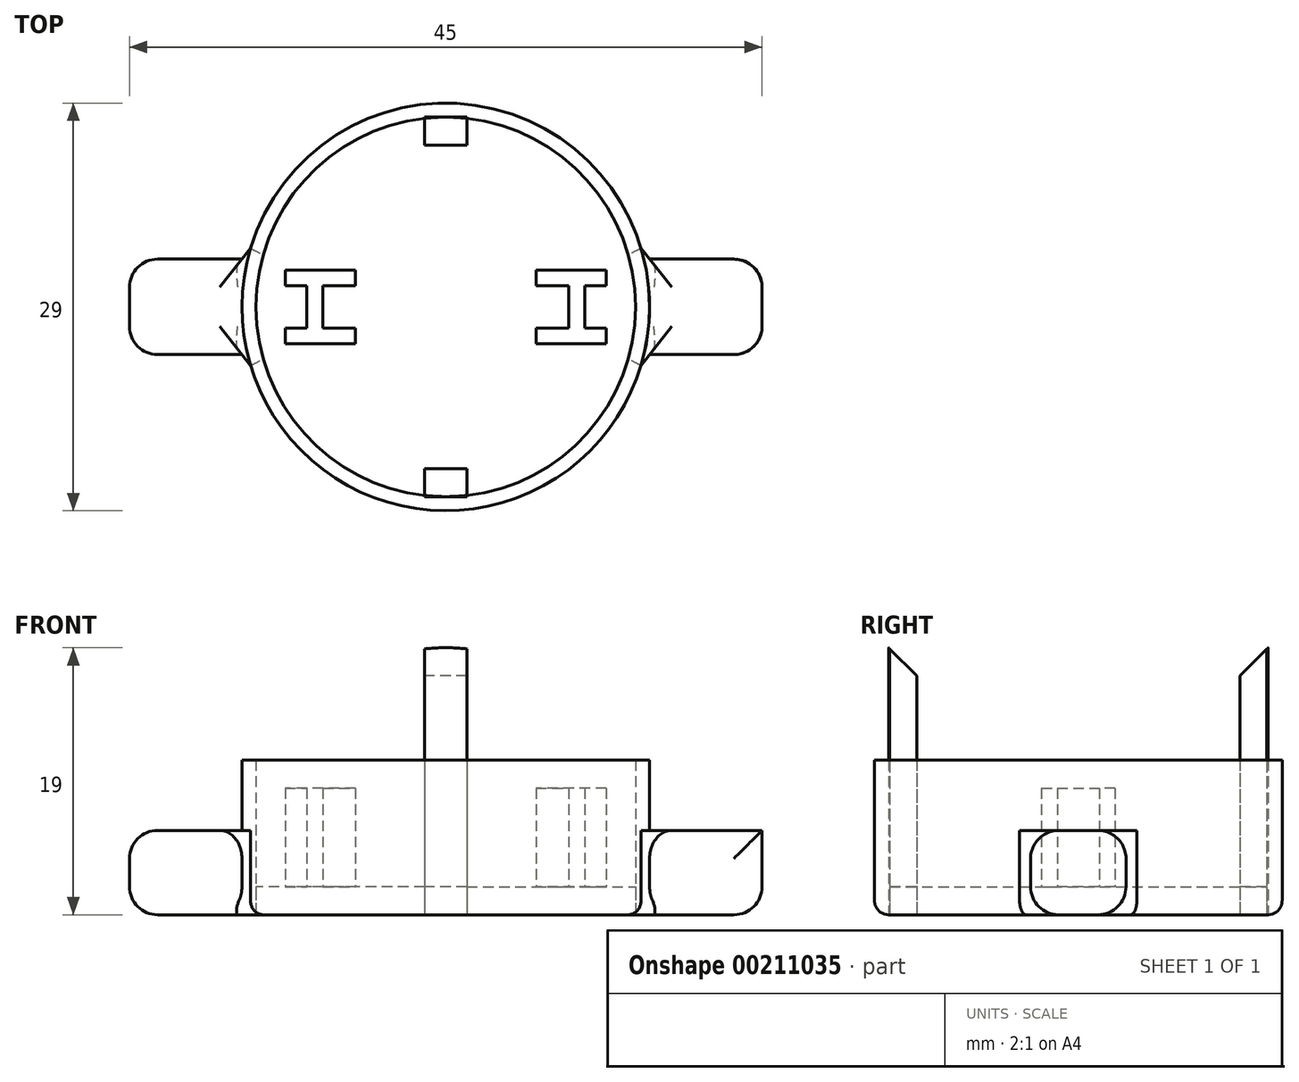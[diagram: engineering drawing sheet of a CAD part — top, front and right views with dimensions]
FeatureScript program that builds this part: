
annotation { "Feature Type Name" : "Feature", "Feature Type Description" : "" }
export const myFeature = defineFeature(function(context is Context, id is Id, definition is map)
    precondition{}
    {
        {
            var Q0;
            Q0=qCreatedBy(makeId("Top.planeOp"),FACE);
            var sketch = newSketch(context, id + "F0", { "sketchPlane" : qUnion([Q0])});
            skCircle(sketch, "E0", {"center": v(0, 0) * mm, "radius": 14.5 * mm});
            skCircle(sketch, "E1", {"center": v(0, 0) * mm, "radius": 13.5 * mm});
            skLineSegment(sketch, "E2", {"start": v(0, 13.5) * mm, "end": v(1.5, 13.5) * mm});
            skLineSegment(sketch, "E3", {"start": v(1.5, 13.5) * mm, "end": v(1.5, 11.5) * mm});
            skLineSegment(sketch, "E4", {"start": v(1.5, 11.5) * mm, "end": v(-1.5, 11.5) * mm});
            skLineSegment(sketch, "E5", {"start": v(-1.5, 11.5) * mm, "end": v(-1.5, 13.5) * mm});
            skLineSegment(sketch, "E6", {"start": v(-1.5, 13.5) * mm, "end": v(0, 13.5) * mm});
            skLineSegment(sketch, "E7", {"start": v(0, -13.5) * mm, "end": v(1.5, -13.5) * mm});
            skLineSegment(sketch, "E8", {"start": v(1.5, -13.5) * mm, "end": v(1.5, -11.5) * mm});
            skLineSegment(sketch, "E9", {"start": v(1.5, -11.5) * mm, "end": v(-1.5, -11.5) * mm});
            skLineSegment(sketch, "E10", {"start": v(-1.5, -11.5) * mm, "end": v(-1.5, -13.5) * mm});
            skLineSegment(sketch, "E11", {"start": v(-1.5, -13.5) * mm, "end": v(0, -13.5) * mm});
            skLineSegment(sketch, "E12", {"start": v(0, 15.56) * mm, "end": v(0, -16.2) * mm, "construction": true});
            skLineSegment(sketch, "E13", {"start": v(-9.9, 0) * mm, "end": v(-9.9, 1.5) * mm});
            skLineSegment(sketch, "E14", {"start": v(-9.9, 1.5) * mm, "end": v(-11.42, 1.5) * mm});
            skLineSegment(sketch, "E15", {"start": v(-11.42, 1.5) * mm, "end": v(-11.42, 2.62) * mm});
            skLineSegment(sketch, "E16", {"start": v(-11.42, 2.62) * mm, "end": v(-6.42, 2.62) * mm});
            skLineSegment(sketch, "E17", {"start": v(-6.42, 2.62) * mm, "end": v(-6.42, 1.5) * mm});
            skLineSegment(sketch, "E18", {"start": v(-6.42, 1.5) * mm, "end": v(-8.75, 1.5) * mm});
            skLineSegment(sketch, "E19", {"start": v(-8.75, 1.5) * mm, "end": v(-8.75, -1.5) * mm});
            skLineSegment(sketch, "E20", {"start": v(-8.75, -1.5) * mm, "end": v(-6.42, -1.5) * mm});
            skLineSegment(sketch, "E21", {"start": v(-6.42, -1.5) * mm, "end": v(-6.42, -2.62) * mm});
            skLineSegment(sketch, "E22", {"start": v(-6.42, -2.62) * mm, "end": v(-11.42, -2.62) * mm});
            skLineSegment(sketch, "E23", {"start": v(-11.42, -2.62) * mm, "end": v(-11.42, -1.5) * mm});
            skLineSegment(sketch, "E24", {"start": v(-11.42, -1.5) * mm, "end": v(-9.9, -1.5) * mm});
            skLineSegment(sketch, "E25", {"start": v(-9.9, -1.5) * mm, "end": v(-9.9, 0) * mm});
            skLineSegment(sketch, "E26.MirrorCS", {"start": v(9.9, 1.5) * mm, "end": v(11.42, 1.5) * mm});
            skLineSegment(sketch, "E27.MirrorCS", {"start": v(9.9, 0) * mm, "end": v(9.9, 1.5) * mm});
            skLineSegment(sketch, "E28.MirrorCS", {"start": v(11.42, 2.62) * mm, "end": v(6.42, 2.62) * mm});
            skLineSegment(sketch, "E29.MirrorCS", {"start": v(6.42, 1.5) * mm, "end": v(8.75, 1.5) * mm});
            skLineSegment(sketch, "E30.MirrorCS", {"start": v(8.75, -1.5) * mm, "end": v(6.42, -1.5) * mm});
            skLineSegment(sketch, "E31.MirrorCS", {"start": v(6.42, -2.62) * mm, "end": v(11.42, -2.62) * mm});
            skLineSegment(sketch, "E32.MirrorCS", {"start": v(11.42, -2.62) * mm, "end": v(11.42, -1.5) * mm});
            skLineSegment(sketch, "E33.MirrorCS", {"start": v(11.42, -1.5) * mm, "end": v(9.9, -1.5) * mm});
            skLineSegment(sketch, "E34.MirrorCS", {"start": v(6.42, -1.5) * mm, "end": v(6.42, -2.62) * mm});
            skLineSegment(sketch, "E35.MirrorCS", {"start": v(9.9, -1.5) * mm, "end": v(9.9, 0) * mm});
            skLineSegment(sketch, "E36.MirrorCS", {"start": v(11.42, 1.5) * mm, "end": v(11.42, 2.62) * mm});
            skLineSegment(sketch, "E37.MirrorCS", {"start": v(6.42, 2.62) * mm, "end": v(6.42, 1.5) * mm});
            skLineSegment(sketch, "E38.MirrorCS", {"start": v(8.75, 1.5) * mm, "end": v(8.75, -1.5) * mm});
            skLineSegment(sketch, "E39", {"start": v(-14.5, 0) * mm, "end": v(-14.5, 3.4) * mm});
            skLineSegment(sketch, "E40", {"start": v(-14.5, 3.4) * mm, "end": v(-22.5, 3.4) * mm});
            skLineSegment(sketch, "E41", {"start": v(-22.5, 3.4) * mm, "end": v(-22.5, -3.4) * mm});
            skLineSegment(sketch, "E42", {"start": v(-22.5, -3.4) * mm, "end": v(-14.5, -3.4) * mm});
            skLineSegment(sketch, "E43", {"start": v(-14.5, -3.4) * mm, "end": v(-14.5, 0) * mm});
            skLineSegment(sketch, "E44", {"start": v(-14.5, -3.4) * mm, "end": v(-13.89, -4.18) * mm});
            skLineSegment(sketch, "E45", {"start": v(-14.5, 3.4) * mm, "end": v(-13.89, 4.17) * mm});
            skLineSegment(sketch, "E46.MirrorCS", {"start": v(14.5, 3.4) * mm, "end": v(13.89, 4.17) * mm});
            skLineSegment(sketch, "E47.MirrorCS", {"start": v(14.5, 3.4) * mm, "end": v(22.5, 3.4) * mm});
            skLineSegment(sketch, "E48.MirrorCS", {"start": v(14.5, 0) * mm, "end": v(14.5, 3.4) * mm});
            skLineSegment(sketch, "E49.MirrorCS", {"start": v(22.5, 3.4) * mm, "end": v(22.5, -3.4) * mm});
            skLineSegment(sketch, "E50.MirrorCS", {"start": v(22.5, -3.4) * mm, "end": v(14.5, -3.4) * mm});
            skLineSegment(sketch, "E51.MirrorCS", {"start": v(14.5, -3.4) * mm, "end": v(14.5, 0) * mm});
            skLineSegment(sketch, "E52.MirrorCS", {"start": v(14.5, -3.4) * mm, "end": v(13.89, -4.18) * mm});
            skSolve(sketch);
        }
        {
            var Q0;
            Q0=makeQuery(id+"F0.imprint","IMPRINT",FACE,{"disambiguationData":[TD([[makeQuery(id+"F0.imprint","IMPRINT",EDGE,{"derivedFrom":sQuery(id+"F0.wireOp",EDGE,"E13")}),-1.0]])]});
            var Q1;
            {var subQ4=sQuery(id+"F0.wireOp",EDGE,"E4");Q1=makeQuery(id+"F0.imprint","IMPRINT",FACE,{"disambiguationData":[TD([[makeQuery(id+"F0.imprint","IMPRINT",EDGE,{"derivedFrom":subQ4}),1.0]])]});}
            var Q2;
            Q2=makeQuery(id+"F0.imprint","IMPRINT",FACE,{"disambiguationData":[TD([[makeQuery(id+"F0.imprint","IMPRINT",EDGE,{"derivedFrom":sQuery(id+"F0.wireOp",EDGE,"E26.MirrorCS")}),1.0]])]});
            extrude(context, id + "F1", {"entities" : qUnion([Q0, Q1, Q2]), "depth" : 2 * mm});
        }
        {
            var Q0;
            {var subQ1=sQuery(id+"F0.wireOp",EDGE,"E2");Q0=makeQuery(id+"F0.imprint","IMPRINT",FACE,{"disambiguationData":[TD([[makeQuery(id+"F0.imprint","IMPRINT",EDGE,{"derivedFrom":subQ1}),1.0]])]});}
            var Q1;
            Q1=makeQuery(id+"F1.opExtrude","CAP_FACE",FACE,{"disambiguationData":[OSD([sQuery(id+"F0.wireOp",EDGE,"E1")])],"isStart":false});
            extrude(context, id + "F2", {"entities" : qUnion([Q0]), "depth" : 11 * mm});
        }
        {
            var Q0;
            Q0=makeQuery(id+"F0.imprint","IMPRINT",FACE,{"disambiguationData":[TD([[makeQuery(id+"F0.imprint","IMPRINT",EDGE,{"derivedFrom":sQuery(id+"F0.wireOp",EDGE,"E13")}),-1.0]])]});
            var Q1;
            Q1=makeQuery(id+"F0.imprint","IMPRINT",FACE,{"disambiguationData":[TD([[makeQuery(id+"F0.imprint","IMPRINT",EDGE,{"derivedFrom":sQuery(id+"F0.wireOp",EDGE,"E26.MirrorCS")}),1.0]])]});
            extrude(context, id + "F3", {"entities" : qUnion([Q0, Q1]), "operationType" : NewBodyOperationType.ADD, "depth" : 9 * mm});
        }
        {
            var Q0;
            {var subQ0=sQuery(id+"F0.wireOp",EDGE,"E9");Q0=makeQuery(id+"F0.imprint","IMPRINT",FACE,{"disambiguationData":[TD([[makeQuery(id+"F0.imprint","IMPRINT",EDGE,{"derivedFrom":subQ0}),1.0]])]});}
            var Q1;
            {var subQ0=sQuery(id+"F0.wireOp",EDGE,"E4");Q1=makeQuery(id+"F0.imprint","IMPRINT",FACE,{"disambiguationData":[TD([[makeQuery(id+"F0.imprint","IMPRINT",EDGE,{"derivedFrom":subQ0}),-1.0]])]});}
            var Q2;
            Q2=makeQuery(id+"F1.opExtrude","CAP_FACE",FACE,{"disambiguationData":[OSD([sQuery(id+"F0.wireOp",EDGE,"E1")])],"isStart":false});
            var Q3;
            Q3=makeQuery(id+"F1.opExtrude","SWEPT_BODY",BODY,{"disambiguationData":[OSD([sQuery(id+"F0.wireOp",EDGE,"E1")])]});
            extrude(context, id + "F4", {"entities" : qUnion([Q0, Q1]), "depth" : 19 * mm});
        }
        {
            var Q0;
            Q0=makeQuery(id+"F0.imprint","IMPRINT",FACE,{"disambiguationData":[TD([[makeQuery(id+"F0.imprint","IMPRINT",EDGE,{"derivedFrom":sQuery(id+"F0.wireOp",EDGE,"E39")}),1.0]])]});
            var Q1;
            Q1=makeQuery(id+"F0.imprint","IMPRINT",FACE,{"disambiguationData":[TD([[makeQuery(id+"F0.imprint","IMPRINT",EDGE,{"derivedFrom":sQuery(id+"F0.wireOp",EDGE,"E47.MirrorCS")}),-1.0]])]});
            var Q2;
            {var subQ0=sQuery(id+"F0.wireOp",EDGE,"E43");Q2=makeQuery(id+"F0.imprint","IMPRINT",FACE,{"disambiguationData":[TD([[makeQuery(id+"F0.imprint","IMPRINT",EDGE,{"derivedFrom":subQ0}),-1.0]])]});}
            var Q3;
            {var subQ0=sQuery(id+"F0.wireOp",EDGE,"E39");Q3=makeQuery(id+"F0.imprint","IMPRINT",FACE,{"disambiguationData":[TD([[makeQuery(id+"F0.imprint","IMPRINT",EDGE,{"derivedFrom":subQ0}),-1.0]])]});}
            var Q4;
            {var subQ0=sQuery(id+"F0.wireOp",EDGE,"E51.MirrorCS");Q4=makeQuery(id+"F0.imprint","IMPRINT",FACE,{"disambiguationData":[TD([[makeQuery(id+"F0.imprint","IMPRINT",EDGE,{"derivedFrom":subQ0}),1.0]])]});}
            var Q5;
            {var subQ0=sQuery(id+"F0.wireOp",EDGE,"E46.MirrorCS");Q5=makeQuery(id+"F0.imprint","IMPRINT",FACE,{"disambiguationData":[TD([[makeQuery(id+"F0.imprint","IMPRINT",EDGE,{"derivedFrom":subQ0}),1.0]])]});}
            extrude(context, id + "F5", {"entities" : qUnion([Q0, Q1, Q2, Q3, Q4, Q5]), "operationType" : NewBodyOperationType.ADD, "depth" : 6 * mm});
        }
        {
            var Q0;
            Q0=makeQuery(id+"F4.opExtrude","CAP_EDGE",EDGE,{"disambiguationData":[OSD([sQuery(id+"F0.wireOp",EDGE,"E4")])],"isStart":false});
            var Q1;
            Q1=makeQuery(id+"F4.opExtrude","CAP_EDGE",EDGE,{"disambiguationData":[OSD([sQuery(id+"F0.wireOp",EDGE,"E9")])],"isStart":false});
            chamfer(context, id + "F6", {"entities" : qUnion([Q0, Q1]), "width" : 2 * mm, "tangentPropagation" : true});
        }
        {
            var Q0;
            {var subQ0=sQuery(id+"F0.wireOp",EDGE,"E44");var subQ1=sQuery(id+"F0.wireOp",EDGE,"E0");Q0=makeQuery(id+"F5.boolean.opBoolean","SPLIT",EDGE,{"disambiguationData":[TD([makeQuery(id+"F5.opExtrude","SWEPT_FACE",FACE,{"disambiguationData":[OSD([subQ0])]})])],"derivedFrom":makeQuery(id+"F2.opExtrude","CAP_EDGE",EDGE,{"disambiguationData":[OSD([subQ1])],"isStart":true})});}
            fillet(context, id + "F7", {"entities" : qUnion([Q0]), "radius" : 1 * mm, "tangentPropagation" : true, "allowEdgeOverflow" : false});
        }
        {
            var Q0;
            {var subQ0=sQuery(id+"F0.wireOp",EDGE,"E45");var subQ1=sQuery(id+"F0.wireOp",EDGE,"E0");Q0=makeQuery(id+"F5.boolean.opBoolean","SPLIT",EDGE,{"disambiguationData":[TD([makeQuery(id+"F5.opExtrude","SWEPT_FACE",FACE,{"disambiguationData":[OSD([subQ0])]})])],"derivedFrom":makeQuery(id+"F2.opExtrude","CAP_EDGE",EDGE,{"disambiguationData":[OSD([subQ1])],"isStart":true})});}
            fillet(context, id + "F8", {"entities" : qUnion([Q0]), "radius" : 1 * mm, "tangentPropagation" : true, "allowEdgeOverflow" : false});
        }
        {
            var Q0;
            Q0=makeQuery(id+"F5.opExtrude","CAP_EDGE",EDGE,{"disambiguationData":[OSD([sQuery(id+"F0.wireOp",EDGE,"E45")])],"isStart":true});
            var Q1;
            Q1=makeQuery(id+"F5.opExtrude","CAP_EDGE",EDGE,{"disambiguationData":[OSD([sQuery(id+"F0.wireOp",EDGE,"E44")])],"isStart":true});
            var Q2;
            Q2=makeQuery(id+"F5.opExtrude","CAP_EDGE",EDGE,{"disambiguationData":[OSD([sQuery(id+"F0.wireOp",EDGE,"E52.MirrorCS")])],"isStart":true});
            var Q3;
            Q3=makeQuery(id+"F5.opExtrude","CAP_EDGE",EDGE,{"disambiguationData":[OSD([sQuery(id+"F0.wireOp",EDGE,"E46.MirrorCS")])],"isStart":true});
            fillet(context, id + "F9", {"entities" : qUnion([Q0, Q1, Q2, Q3]), "radius" : 1 * mm, "tangentPropagation" : true, "allowEdgeOverflow" : false});
        }
        {
            var Q0;
            Q0=makeQuery(id+"F5.opExtrude","CAP_EDGE",EDGE,{"disambiguationData":[OSD([sQuery(id+"F0.wireOp",EDGE,"E50.MirrorCS")])],"isStart":true});
            var Q1;
            Q1=makeQuery(id+"F5.opExtrude","CAP_EDGE",EDGE,{"disambiguationData":[OSD([sQuery(id+"F0.wireOp",EDGE,"E49.MirrorCS")])],"isStart":true});
            var Q2;
            Q2=makeQuery(id+"F5.opExtrude","CAP_EDGE",EDGE,{"disambiguationData":[OSD([sQuery(id+"F0.wireOp",EDGE,"E47.MirrorCS")])],"isStart":true});
            var Q3;
            Q3=makeQuery(id+"F5.opExtrude","CAP_EDGE",EDGE,{"disambiguationData":[OSD([sQuery(id+"F0.wireOp",EDGE,"E40")])],"isStart":true});
            var Q4;
            Q4=makeQuery(id+"F5.opExtrude","CAP_EDGE",EDGE,{"disambiguationData":[OSD([sQuery(id+"F0.wireOp",EDGE,"E42")])],"isStart":true});
            var Q5;
            Q5=makeQuery(id+"F5.opExtrude","CAP_EDGE",EDGE,{"disambiguationData":[OSD([sQuery(id+"F0.wireOp",EDGE,"E41")])],"isStart":true});
            var Q6;
            Q6=makeQuery(id+"F5.opExtrude","SWEPT_EDGE",EDGE,{"disambiguationData":[OSD([sQuery(id+"F0.wireOp",EDGE,"E47.MirrorCS"),sQuery(id+"F0.wireOp",EDGE,"E49.MirrorCS")])]});
            var Q7;
            Q7=makeQuery(id+"F5.opExtrude","CAP_EDGE",EDGE,{"disambiguationData":[OSD([sQuery(id+"F0.wireOp",EDGE,"E47.MirrorCS")])],"isStart":false});
            var Q8;
            Q8=makeQuery(id+"F5.opExtrude","CAP_EDGE",EDGE,{"disambiguationData":[OSD([sQuery(id+"F0.wireOp",EDGE,"E40")])],"isStart":false});
            var Q9;
            Q9=makeQuery(id+"F5.opExtrude","SWEPT_EDGE",EDGE,{"disambiguationData":[OSD([sQuery(id+"F0.wireOp",EDGE,"E40"),sQuery(id+"F0.wireOp",EDGE,"E41")])]});
            var Q10;
            Q10=makeQuery(id+"F5.opExtrude","CAP_EDGE",EDGE,{"disambiguationData":[OSD([sQuery(id+"F0.wireOp",EDGE,"E41")])],"isStart":false});
            var Q11;
            Q11=makeQuery(id+"F5.opExtrude","SWEPT_EDGE",EDGE,{"disambiguationData":[OSD([sQuery(id+"F0.wireOp",EDGE,"E41"),sQuery(id+"F0.wireOp",EDGE,"E42")])]});
            var Q12;
            Q12=makeQuery(id+"F5.opExtrude","SWEPT_EDGE",EDGE,{"disambiguationData":[OSD([sQuery(id+"F0.wireOp",EDGE,"E49.MirrorCS"),sQuery(id+"F0.wireOp",EDGE,"E50.MirrorCS")])]});
            var Q13;
            Q13=makeQuery(id+"F5.opExtrude","CAP_EDGE",EDGE,{"disambiguationData":[OSD([sQuery(id+"F0.wireOp",EDGE,"E50.MirrorCS")])],"isStart":false});
            var Q14;
            Q14=makeQuery(id+"F5.opExtrude","CAP_EDGE",EDGE,{"disambiguationData":[OSD([sQuery(id+"F0.wireOp",EDGE,"E42")])],"isStart":false});
            fillet(context, id + "F10", {"entities" : qUnion([Q0, Q1, Q2, Q3, Q4, Q5, Q6, Q7, Q8, Q9, Q10, Q11, Q12, Q13, Q14]), "radius" : 2 * mm, "tangentPropagation" : true, "allowEdgeOverflow" : false});
        }
    });
